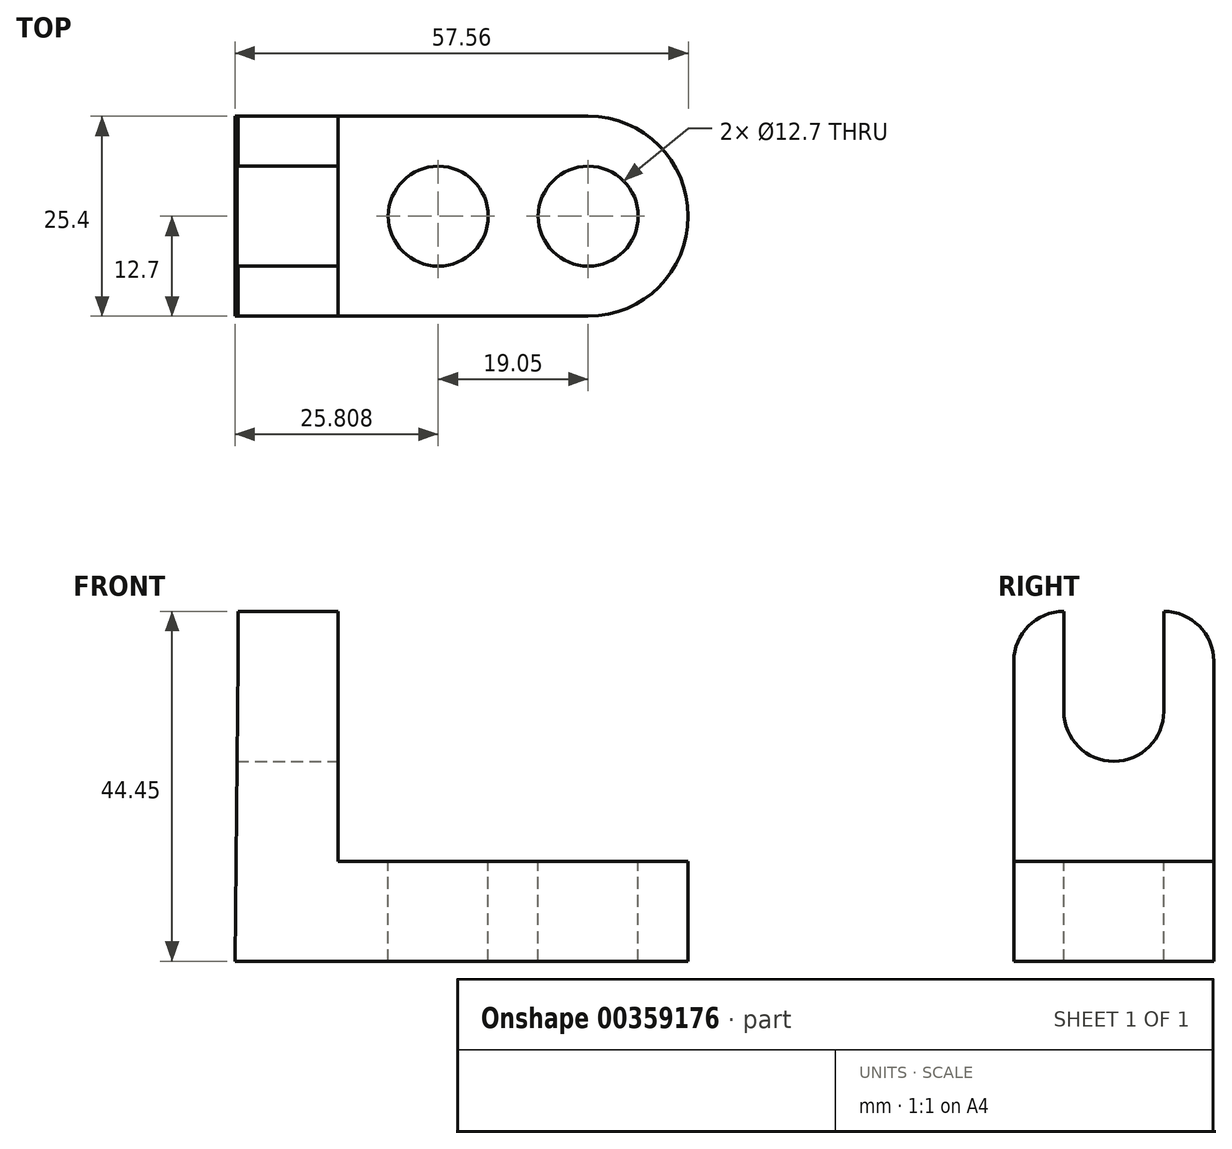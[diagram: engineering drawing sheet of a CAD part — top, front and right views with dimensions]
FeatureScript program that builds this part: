
annotation { "Feature Type Name" : "Feature", "Feature Type Description" : "" }
export const myFeature = defineFeature(function(context is Context, id is Id, definition is map)
    precondition{}
    {
        {
            var Q0;
            Q0=qCreatedBy(makeId("Front.planeOp"),FACE);
            var sketch = newSketch(context, id + "F0", { "sketchPlane" : qUnion([Q0])});
            skLineSegment(sketch, "E0", {"start": v(-35.11, 32.6) * mm, "end": v(-22.41, 32.6) * mm});
            skLineSegment(sketch, "E1", {"start": v(-22.41, 32.6) * mm, "end": v(-22.41, 0.84) * mm});
            skLineSegment(sketch, "E2", {"start": v(-22.41, 0.84) * mm, "end": v(22.04, 0.84) * mm});
            skLineSegment(sketch, "E3", {"start": v(22.04, 0.84) * mm, "end": v(22.04, -11.86) * mm});
            skLineSegment(sketch, "E4", {"start": v(22.04, -11.86) * mm, "end": v(-35.52, -11.86) * mm});
            skLineSegment(sketch, "E5", {"start": v(-35.52, -11.86) * mm, "end": v(-35.11, 32.6) * mm});
            skSolve(sketch);
        }
        {
            var Q0;
            Q0=makeQuery(id+"F0.imprint","IMPRINT",FACE,{"disambiguationData":[TD([[makeQuery(id+"F0.imprint","IMPRINT",EDGE,{"derivedFrom":sQuery(id+"F0.wireOp",EDGE,"E0")}),-1.0]])]});
            extrude(context, id + "F1", {"entities" : qUnion([Q0]), "depth" : 25.4 * mm});
        }
        {
            var Q0;
            Q0=makeQuery(id+"F1.opExtrude","SWEPT_FACE",FACE,{"disambiguationData":[OSD([sQuery(id+"F0.wireOp",EDGE,"E2")])]});
            var sketch = newSketch(context, id + "F2", { "sketchPlane" : qUnion([Q0])});
            skLineSegment(sketch, "E6", {"start": v(0, 0) * mm, "end": v(9.34, 0) * mm});
            skLineSegment(sketch, "E7", {"start": v(22.04, -12.7) * mm, "end": v(22.04, -12.7) * mm});
            skLineSegment(sketch, "E8", {"start": v(9.34, -25.4) * mm, "end": v(0, -25.4) * mm});
            skPoint(sketch, "E9.visualSharp", {"position": v(22.04, 0) * mm});
            skArc(sketch, "E9.filletArc", {"start": v(22.04, -12.7) * mm, "mid": v(18.32, -3.72) * mm, "end": v(9.34, 0) * mm});
            skPoint(sketch, "E10.visualSharp", {"position": v(22.04, -25.4) * mm});
            skArc(sketch, "E10.filletArc", {"start": v(9.34, -25.4) * mm, "mid": v(18.32, -21.68) * mm, "end": v(22.04, -12.7) * mm});
            skCircle(sketch, "E11", {"center": v(9.34, -12.7) * mm, "radius": 6.35 * mm});
            skCircle(sketch, "E12", {"center": v(-9.71, -12.7) * mm, "radius": 6.35 * mm});
            skSolve(sketch);
        }
        {
            var Q0;
            Q0=makeQuery(id+"F2.imprint","IMPRINT",FACE,{"disambiguationData":[TD([[makeQuery(id+"F2.imprint","IMPRINT",EDGE,{"derivedFrom":sQuery(id+"F2.wireOp",EDGE,"E12")}),1.0]])]});
            var Q1;
            Q1=makeQuery(id+"F2.imprint","IMPRINT",FACE,{"disambiguationData":[TD([[makeQuery(id+"F2.imprint","IMPRINT",EDGE,{"derivedFrom":sQuery(id+"F2.wireOp",EDGE,"E11")}),1.0]])]});
            var Q2;
            {var subQ0=sQuery(id+"F2.wireOp",EDGE,"E9.filletArc");Q2=makeQuery(id+"F2.imprint","IMPRINT",FACE,{"disambiguationData":[TD([[makeQuery(id+"F2.imprint","IMPRINT",EDGE,{"derivedFrom":subQ0}),-1.0]])]});}
            var Q3;
            {var subQ0=sQuery(id+"F2.wireOp",EDGE,"E10.filletArc");Q3=makeQuery(id+"F2.imprint","IMPRINT",FACE,{"disambiguationData":[TD([[makeQuery(id+"F2.imprint","IMPRINT",EDGE,{"derivedFrom":subQ0}),-1.0]])]});}
            extrude(context, id + "F3", {"entities" : qUnion([Q0, Q1, Q2, Q3]), "operationType" : NewBodyOperationType.REMOVE, "oppositeDirection" : true, "depth" : 25.4 * mm});
        }
        {
            var Q0;
            Q0=makeQuery(id+"F1.opExtrude","SWEPT_FACE",FACE,{"disambiguationData":[OSD([sQuery(id+"F0.wireOp",EDGE,"E1")])]});
            var sketch = newSketch(context, id + "F4", { "sketchPlane" : qUnion([Q0])});
            skLineSegment(sketch, "E13", {"start": v(-19.05, 32.6) * mm, "end": v(-6.35, 32.6) * mm});
            skLineSegment(sketch, "E14", {"start": v(0, 26.24) * mm, "end": v(0, 19.34) * mm});
            skLineSegment(sketch, "E15", {"start": v(-25.4, 26.24) * mm, "end": v(-25.4, 20.9) * mm});
            skPoint(sketch, "E16.visualSharp", {"position": v(-25.4, 32.6) * mm});
            skArc(sketch, "E16.filletArc", {"start": v(-19.05, 32.6) * mm, "mid": v(-23.54, 30.73) * mm, "end": v(-25.4, 26.24) * mm});
            skPoint(sketch, "E17.visualSharp", {"position": v(0, 32.6) * mm});
            skArc(sketch, "E17.filletArc", {"start": v(0, 26.24) * mm, "mid": v(-1.86, 30.73) * mm, "end": v(-6.35, 32.6) * mm});
            skSolve(sketch);
        }
        {
            var Q0;
            {var subQ0=sQuery(id+"F4.wireOp",EDGE,"E16.filletArc");Q0=makeQuery(id+"F4.imprint","IMPRINT",FACE,{"disambiguationData":[TD([[makeQuery(id+"F4.imprint","IMPRINT",EDGE,{"derivedFrom":subQ0}),-1.0]])]});}
            var Q1;
            {var subQ0=sQuery(id+"F4.wireOp",EDGE,"E17.filletArc");Q1=makeQuery(id+"F4.imprint","IMPRINT",FACE,{"disambiguationData":[TD([[makeQuery(id+"F4.imprint","IMPRINT",EDGE,{"derivedFrom":subQ0}),-1.0]])]});}
            extrude(context, id + "F5", {"entities" : qUnion([Q0, Q1]), "operationType" : NewBodyOperationType.REMOVE, "oppositeDirection" : true, "depth" : 25.4 * mm});
        }
        {
            var Q0;
            Q0=makeQuery(id+"F1.opExtrude","SWEPT_FACE",FACE,{"disambiguationData":[OSD([sQuery(id+"F0.wireOp",EDGE,"E1")])]});
            var sketch = newSketch(context, id + "F6", { "sketchPlane" : qUnion([Q0])});
            skCircle(sketch, "E18", {"center": v(-12.7, 19.9) * mm, "radius": 6.35 * mm});
            skLineSegment(sketch, "E19", {"start": v(-19.05, 19.9) * mm, "end": v(-19.05, 32.6) * mm});
            skLineSegment(sketch, "E20", {"start": v(-6.35, 19.9) * mm, "end": v(-6.35, 32.6) * mm});
            skSolve(sketch);
        }
        {
            var Q0;
            {var subQ0=sQuery(id+"F6.wireOp",EDGE,"E19");Q0=makeQuery(id+"F6.imprint","IMPRINT",FACE,{"disambiguationData":[TD([[makeQuery(id+"F6.imprint","IMPRINT",EDGE,{"derivedFrom":subQ0}),-1.0]])]});}
            var Q1;
            {var subQ0=sQuery(id+"F6.wireOp",EDGE,"E18");var subQ1=makeQuery(id+"F6.imprint","INTERSECT",VERTEX,{"derivedFrom":[subQ0,sQuery(id+"F6.wireOp",EDGE,"E19")]});Q1=makeQuery(id+"F6.imprint","IMPRINT",FACE,{"disambiguationData":[TD([[makeQuery(id+"F6.imprint","IMPRINT",EDGE,{"disambiguationData":[TD([[subQ1,1.0]])],"derivedFrom":subQ0}),1.0]])]});}
            extrude(context, id + "F7", {"entities" : qUnion([Q0, Q1]), "operationType" : NewBodyOperationType.REMOVE, "oppositeDirection" : true, "depth" : 25.4 * mm});
        }
    });
